# Revit family: FU_Chair_Sandler_Hull 1-1
name_source: partatom
category: Furniture
units: mm (PartAtom-declared; Revit-internal decimal feet)

## family parameters
Always vertical = Yes
Cut with Voids When Loaded = No
OmniClass Number = 23.40.20.00
OmniClass Title = General Furniture and Specialties
Room Calculation Point = No
Shared = No
Work Plane-Based = No

## types (1)
- Hull 1.1
    Default Elevation = 0 mm  [stored 0 ft]
    Depth = 490 mm  [stored 1.60761 ft]
    Description = Chair with 4 legs steel frame. Beech wood seat and back.
    Frame = Metal - Paint -AL VR - White Aluminium
    Height = 770 mm  [stored 2.52625 ft]
    Manufacturer = Sandler
    Model = Hull 1.1
    Seat = Wood - Beech - Chestnut Stain
    URL = https://www.sandlerseating.com
    Width = 480 mm  [stored 1.5748 ft]

note: [stored X ft] marks values corroborated as IEEE doubles in the binary element streams (Revit-internal decimal feet)

## geometry (parser evidence)
native form markers: Sweep x8
no freeform markers — native parametric forms only
